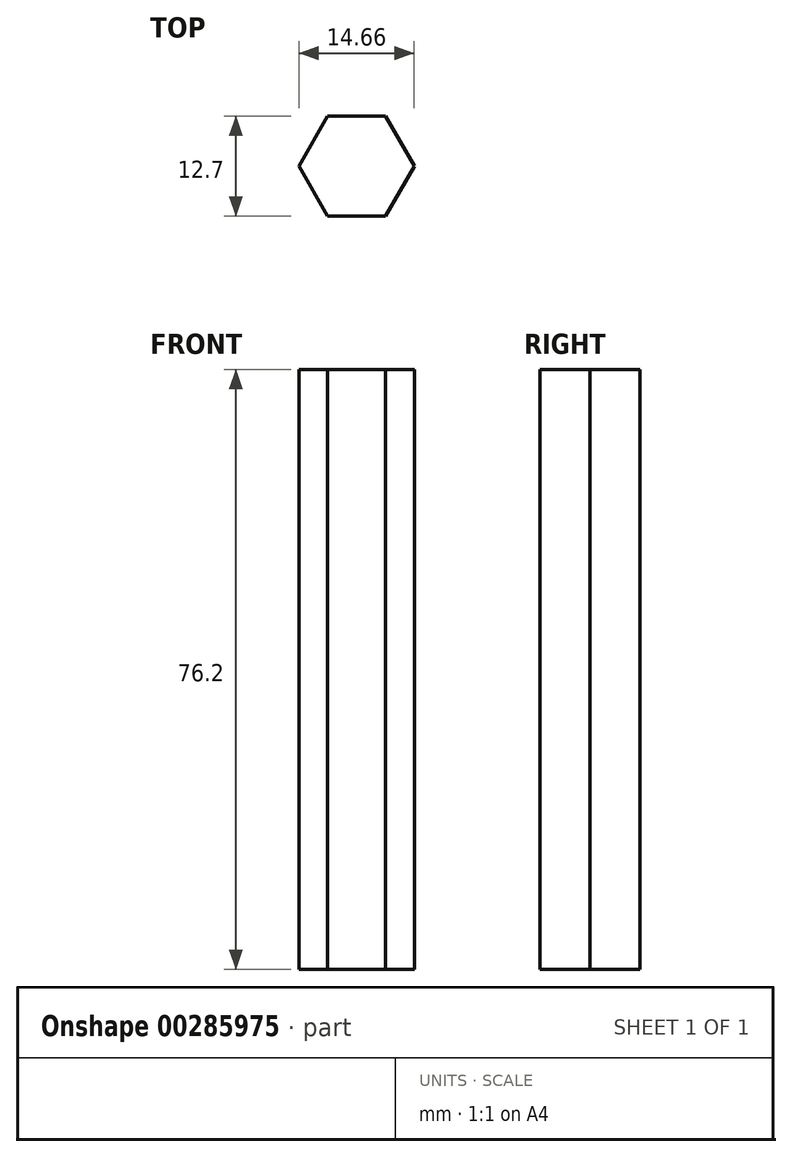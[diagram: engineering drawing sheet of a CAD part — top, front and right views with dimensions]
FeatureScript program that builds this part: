
annotation { "Feature Type Name" : "Feature", "Feature Type Description" : "" }
export const myFeature = defineFeature(function(context is Context, id is Id, definition is map)
    precondition{}
    {
        {
            var Q0;
            Q0=qCreatedBy(makeId("Top.planeOp"),FACE);
            var sketch = newSketch(context, id + "F0", { "sketchPlane" : qUnion([Q0])});
            skCircle(sketch, "E0.cCircle", {"center": v(0, 0) * mm, "radius": 6.35 * mm, "construction": true});
            skLineSegment(sketch, "E0.0", {"start": v(-7.33, 0) * mm, "end": v(-3.67, 6.35) * mm});
            skLineSegment(sketch, "E0.1", {"start": v(-3.67, 6.35) * mm, "end": v(3.67, 6.35) * mm});
            skLineSegment(sketch, "E0.2", {"start": v(3.67, 6.35) * mm, "end": v(7.33, 0) * mm});
            skLineSegment(sketch, "E0.3", {"start": v(7.33, 0) * mm, "end": v(3.67, -6.35) * mm});
            skLineSegment(sketch, "E0.4", {"start": v(3.67, -6.35) * mm, "end": v(-3.67, -6.35) * mm});
            skLineSegment(sketch, "E0.5", {"start": v(-3.67, -6.35) * mm, "end": v(-7.33, 0) * mm});
            skPoint(sketch, "E0.0.midPoint", {"position": v(-5.5, 3.18) * mm});
            skSolve(sketch);
        }
        {
            var Q0;
            Q0 = qSketchRegion(id + "F0", true);
            extrude(context, id + "F1", {"entities" : qUnion([Q0]), "depth" : 76.2 * mm});
        }
    });
